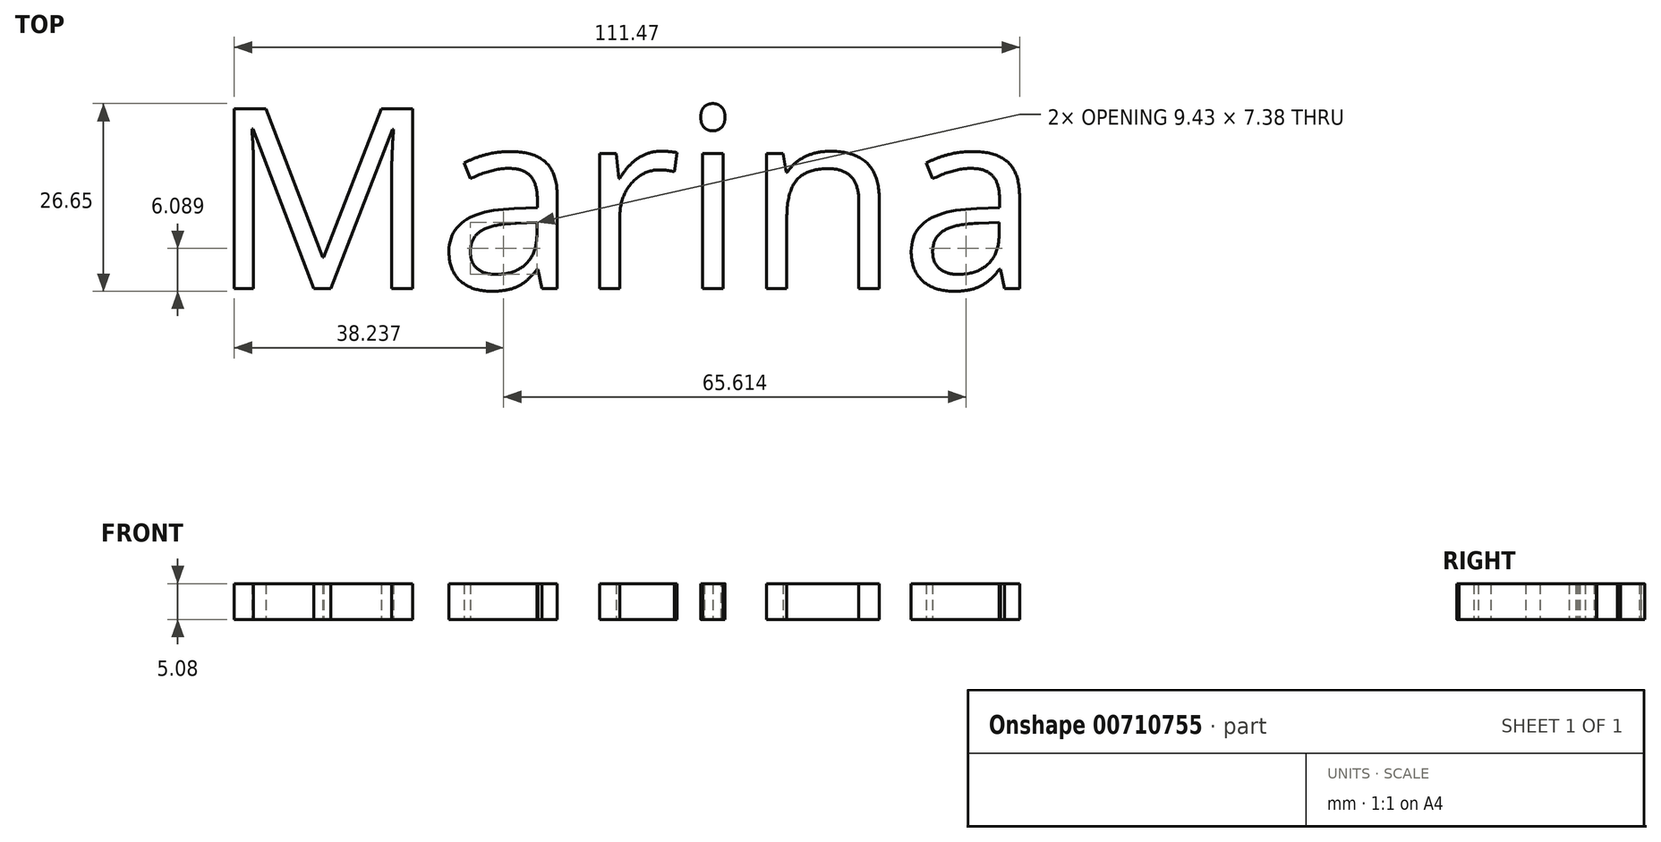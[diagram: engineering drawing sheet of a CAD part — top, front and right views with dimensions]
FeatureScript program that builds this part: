
annotation { "Feature Type Name" : "Feature", "Feature Type Description" : "" }
export const myFeature = defineFeature(function(context is Context, id is Id, definition is map)
    precondition{}
    {
        {
            var Q0;
            Q0=qCreatedBy(makeId("Top.planeOp"),FACE);
            var sketch = newSketch(context, id + "F0", { "sketchPlane" : qUnion([Q0])});
            skText(sketch, "E0", { "text": "Marina", "fontName": "OpenSans-Regular.ttf"});
            skLineSegment(sketch, "E1", {"start": v(-80.76, -11.46) * mm, "end": v(36.6, -11.46) * mm});
            const initialGuessF0  = {"E0": [-0.08076, -0.03727, 1, 0, 0.0258]};
            skSetInitialGuess(sketch, initialGuessF0);
            skSolve(sketch);
        }
        {
            var Q0;
            Q0 = qSketchRegion(id + "F0", true);
            extrude(context, id + "F1", {"entities" : qUnion([Q0]), "depth" : 5.08 * mm, "offsetDistance" : 25.4 * mm});
        }
    });
